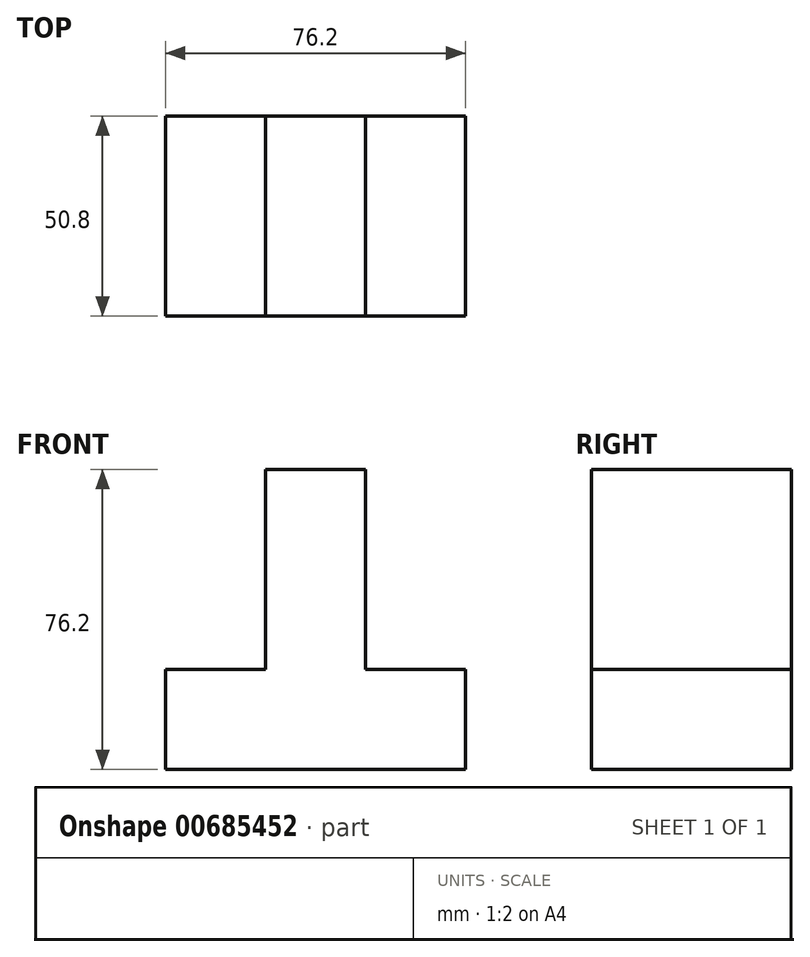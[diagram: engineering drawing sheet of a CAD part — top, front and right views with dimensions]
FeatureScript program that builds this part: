
annotation { "Feature Type Name" : "Feature", "Feature Type Description" : "" }
export const myFeature = defineFeature(function(context is Context, id is Id, definition is map)
    precondition{}
    {
        {
            var Q0;
            Q0=qCreatedBy(makeId("Front.planeOp"),FACE);
            var sketch = newSketch(context, id + "F0", { "sketchPlane" : qUnion([Q0])});
            skLineSegment(sketch, "E0", {"start": v(0, 0) * mm, "end": v(-76.2, 0) * mm});
            skLineSegment(sketch, "E1", {"start": v(-76.2, 0) * mm, "end": v(-76.2, 25.4) * mm});
            skLineSegment(sketch, "E2", {"start": v(-76.2, 25.4) * mm, "end": v(-50.8, 25.4) * mm});
            skLineSegment(sketch, "E3", {"start": v(-50.8, 25.4) * mm, "end": v(-50.8, 76.2) * mm});
            skLineSegment(sketch, "E4", {"start": v(0, 0) * mm, "end": v(0, 25.4) * mm});
            skLineSegment(sketch, "E5", {"start": v(0, 25.4) * mm, "end": v(-25.4, 25.4) * mm});
            skLineSegment(sketch, "E6", {"start": v(-25.4, 25.4) * mm, "end": v(-25.4, 76.2) * mm});
            skLineSegment(sketch, "E7", {"start": v(-25.4, 76.2) * mm, "end": v(-50.8, 76.2) * mm});
            skSolve(sketch);
        }
        {
            var Q0;
            Q0 = qSketchRegion(id + "F0", true);
            extrude(context, id + "F1", {"entities" : qUnion([Q0]), "depth" : 50.8 * mm, "offsetDistance" : 25.4 * mm});
        }
    });
